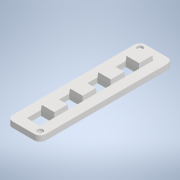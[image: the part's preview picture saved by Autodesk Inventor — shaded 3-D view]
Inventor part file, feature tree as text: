
AUTODESK INVENTOR PART (.ipt)
format: ipt  version: 2020 (Build 240168000, 168)  size: 307,712 bytes
history: native  units: mm
features: chamfer x17, projected_geometry x4, other x3, direct_edit x1, draft x1, extrude x1, sketch x1, move_body x1
ambient origin geometry x8: Origin, YZ Plane, XZ Plane, XY Plane, X Axis, Y Axis, Z Axis, Center Point
bodies: Solid1 (feature_tree)
feature tree (29):
  other  "open_side.ipt"
  direct_edit  "Direct Edit1"
  chamfer  "Chamfer1"  Distance=6.0mm
  chamfer  "Chamfer2"  Distance=2.0mm
  chamfer  "Chamfer3"  Distance=4.0mm
  chamfer  "Chamfer4"  Distance=2.0mm
  chamfer  "Chamfer5"  Distance=4.0mm
  chamfer  "Chamfer6"  Distance=2.0mm
  chamfer  "Chamfer7"  Distance=4.0mm
  chamfer  "Chamfer8"  Distance=2.0mm
  chamfer  "Chamfer9"  Distance=4.0mm
  chamfer  "Chamfer10"  Distance=2.0mm
  chamfer  "Chamfer11"  Distance=4.0mm
  chamfer  "Chamfer12"  Distance=2.0mm
  chamfer  "Chamfer13"  Distance=4.0mm
  chamfer  "Chamfer14"  Distance=2.0mm
  chamfer  "Chamfer15"  Distance=4.0mm
  chamfer  "Chamfer16"  Distance=2.0mm
  draft  "FaceDraft2"
  extrude  "Extrusion1"  Depth=4.0mm
  chamfer  "Chamfer17"  Distance=2.0mm
  other  "Solid1::open_side.ipt"
  other  "TaggingFeature1"
  sketch  "Sketch1"  dims[d0=10.0mm d1=0.0mm d2=0.0mm d3=6.0mm d5=2.0mm d7=4.0mm d8=2.0mm d9=0.872665mm d10=4.0mm d11=2.0mm d12=0.872665mm d13=4.0mm d14=2.0mm d15=0.872665mm d16=4.0mm d17=2.0mm d18=0.872665mm d19=4.0mm d20=2.0mm d21=0.872665mm d22=4.0mm d23=2.0mm d24=0.872665mm d25=4.0mm d26=2.0mm d27=0.872665mm d28=4.0mm d29=2.0mm d30=0.872665mm d31=4.0mm d32=2.0mm d33=0.872665mm d34=4.0mm d35=2.0mm d36=0.872665mm d37=4.0mm d38=2.0mm d39=0.872665mm d40=4.0mm d41=2.0mm d42=0.872665mm d43=4.0mm d44=2.0mm d45=0.872665mm d46=4.0mm d47=2.0mm d48=0.872665mm d49=4.0mm d50=2.0mm d51=0.872665mm d53=0.872665mm d54=0.5mm d55=0.5mm d56=0.5mm d57=0.5mm d58=0.5mm d59=0.5mm d60=0.5mm d61=0.5mm d62=0.5mm d63=0.5mm d64=0.0mm d65=0.5mm d66=2.0mm d67=0.872665mm]
  projected_geometry  "Projected Loop1"
  projected_geometry  "Projected Loop2"
  projected_geometry  "Projected Loop3"
  projected_geometry  "Projected Loop4"
  move_body  "Move1"
